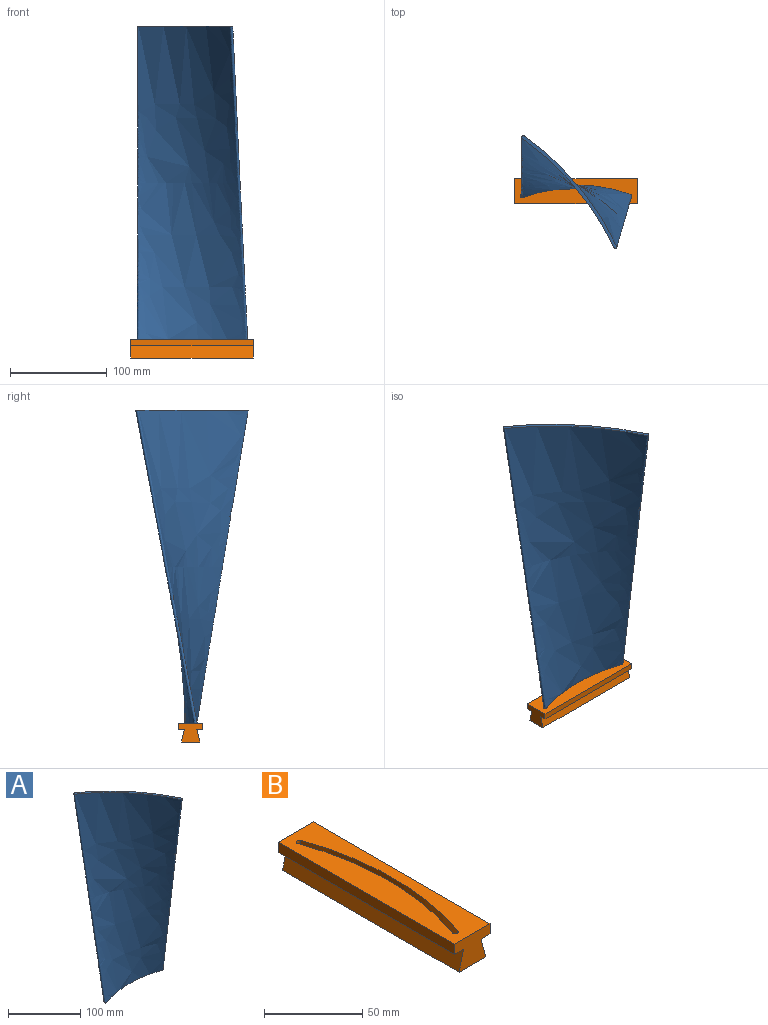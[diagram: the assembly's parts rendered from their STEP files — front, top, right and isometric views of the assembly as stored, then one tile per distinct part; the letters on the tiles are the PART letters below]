
ASSEMBLY  parts=2 mates=1
PART A: 3 faces, bbox 114.2x116.3x323.9 mm
  f0: plane 114.19x12.86mm, normal (0,0,-1), area 367.2mm2, adj f2
  f1: plane 116.3x98.11mm, normal (0,0,1), area 481.7mm2, adj f2
  f2: bspline ~323.85x116.24mm, area 83170.3mm2, adj f0,f1
PART B: 15 faces, bbox 25.4x127x19.1 mm
  f0: plane 127x6.34mm, normal (0,0,-1), area 805.3mm2, adj f1,f7,f8,f9,f11,f13
  f1: plane 127x12.7mm, normal (-0.97,0,0.24), area 1662.3mm2, adj f0,f2,f8,f9,f14
  f2: plane 127x19.05mm, normal (0,0,-1), area 2419.3mm2, adj f1,f3,f8,f9
  f3: plane 127x12.7mm, normal (0.97,0,0.24), area 1662.3mm2, adj f2,f4,f8,f9
  f4: plane 127x6.34mm, normal (0,0,-1), area 805.4mm2, adj f3,f5,f8,f9
  f5: plane 127x6.35mm, normal (1,0,0), area 806.5mm2, adj f4,f6,f8,f9
  f6: plane 127x25.4mm, normal (0,0,1), area 2856mm2, adj f5,f7,f8,f9,f10,f11,f12,f13
  f7: plane 127x6.35mm, normal (-1,0,0), area 806.5mm2, adj f0,f6,f8,f9
  f8: plane 25.4x19.05mm, normal (0,-1,0), area 363mm2, adj f0,f1,f2,f3,f4,f5,f6,f7
  f9: plane 25.4x19.05mm, normal (0,1,0), area 363mm2, adj f0,f1,f2,f3,f4,f5,f6,f7
  f10: cylinder r=168.84mm len=112.85mm, axis (0,0,1), area 730.6mm2, adj f6,f11,f13,f14
  f11: cylinder r=1.59mm len=6.35mm, axis (0,0,1), area 31.7mm2, adj f0,f6,f10,f12,f14
  f12: cylinder r=165.66mm len=110.73mm, axis (0,0,1), area 716.9mm2, adj f6,f11,f13,f14
  f13: cylinder r=1.59mm len=6.35mm, axis (0,0,1), area 31.7mm2, adj f0,f6,f10,f12,f14
  f14: plane 114.96x12.71mm, normal (0,0,1), area 369.7mm2, adj f1,f10,f11,f12,f13
PLACE A t=(-113.32,38.55,-5.57)mm
PLACE B rot(axis=(0,0,1),90deg) t=(-113.75,33.79,-24.62)mm
MATE fastened A.f0 <-> B.f6  axis (0,0,1) through (-58.39,27.44,-5.57)mm
